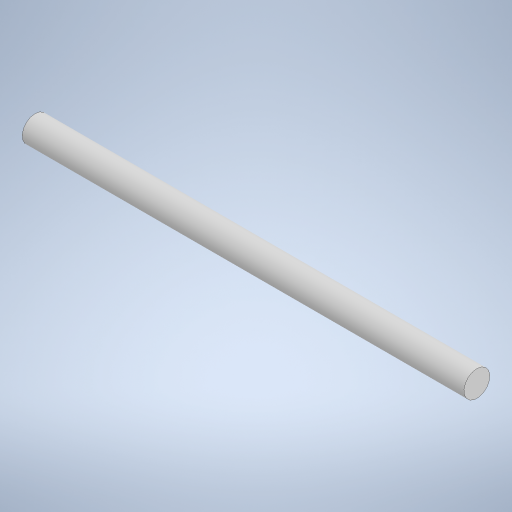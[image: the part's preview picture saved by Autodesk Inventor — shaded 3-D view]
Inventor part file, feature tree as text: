
AUTODESK INVENTOR PART (.ipt)
format: ipt  version: 2024.1 (Build 281209000, 209)  size: 233,472 bytes
history: native  units: mm
features: extrude x1, sketch x1
ambient origin geometry x8: Origin, YZ Plane, XZ Plane, XY Plane, X Axis, Y Axis, Z Axis, Center Point
bodies: Solid1 (feature_tree)
feature tree (2):
  extrude  "Extrusion1"  Depth=75.0mm TaperAngle=0.0deg
  sketch  "Sketch1"  dims[d0=4.4mm d1=75.0mm d2=0.0mm]
